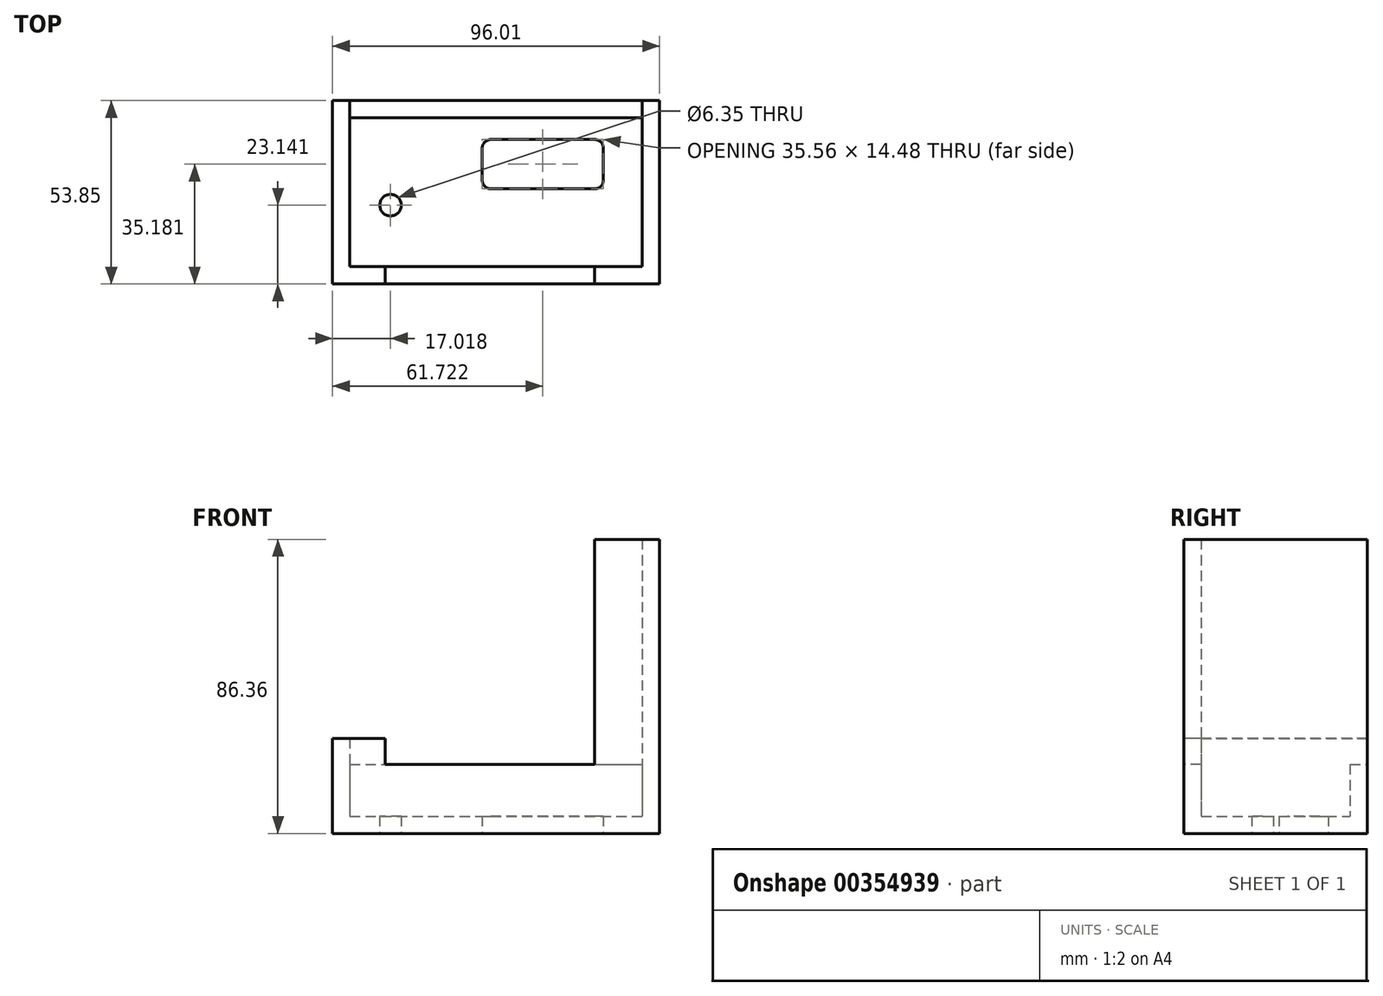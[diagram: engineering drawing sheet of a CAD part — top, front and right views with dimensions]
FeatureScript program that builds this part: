
annotation { "Feature Type Name" : "Feature", "Feature Type Description" : "" }
export const myFeature = defineFeature(function(context is Context, id is Id, definition is map)
    precondition{}
    {
        {
            var Q0;
            Q0=qCreatedBy(makeId("Front.planeOp"),FACE);
            var sketch = newSketch(context, id + "F0", { "sketchPlane" : qUnion([Q0])});
            skLineSegment(sketch, "E0.bottom", {"start": v(0, 86.36) * mm, "end": v(96.01, 86.36) * mm});
            skLineSegment(sketch, "E0.top", {"start": v(0, 0) * mm, "end": v(96.01, 0) * mm});
            skLineSegment(sketch, "E0.left", {"start": v(0, 86.36) * mm, "end": v(0, 0) * mm});
            skLineSegment(sketch, "E0.right", {"start": v(96.01, 86.36) * mm, "end": v(96.01, 0) * mm});
            skSolve(sketch);
        }
        {
            var Q0;
            Q0=makeQuery(id+"F0.imprint","IMPRINT",FACE,{"disambiguationData":[TD([[makeQuery(id+"F0.imprint","IMPRINT",EDGE,{"derivedFrom":sQuery(id+"F0.wireOp",EDGE,"E0.bottom")}),-1.0]])]});
            extrude(context, id + "F1", {"entities" : qUnion([Q0]), "depth" : 53.85 * mm});
        }
        {
            var Q0;
            Q0=makeQuery(id+"F1.opExtrude","SWEPT_FACE",FACE,{"disambiguationData":[OSD([sQuery(id+"F0.wireOp",EDGE,"E0.bottom")])]});
            var Q1;
            Q1=makeQuery(id+"F1.opExtrude","CAP_FACE",FACE,{"disambiguationData":[OSD([sQuery(id+"F0.wireOp",EDGE,"E0.bottom"),sQuery(id+"F0.wireOp",EDGE,"E0.top"),sQuery(id+"F0.wireOp",EDGE,"E0.left"),sQuery(id+"F0.wireOp",EDGE,"E0.right")])],"isStart":true});
            shell(context, id + "F2", {"entities" : qUnion([Q0, Q1]), "thickness" : 5.08 * mm});
        }
        {
            var Q0;
            Q0=makeQuery(id+"F1.opExtrude","SWEPT_FACE",FACE,{"disambiguationData":[OSD([sQuery(id+"F0.wireOp",EDGE,"E0.top")])]});
            var sketch = newSketch(context, id + "F3", { "sketchPlane" : qUnion([Q0])});
            skPoint(sketch, "E1", {"position": v(17.02, 30.7) * mm});
            skSolve(sketch);
        }
        {
            var Q0;
            Q0=sQuery(id+"F3.wireOp",VERTEX,"E1");
            var Q1;
            Q1=makeQuery(id+"F1.opExtrude","SWEPT_BODY",BODY,{"disambiguationData":[OSD([sQuery(id+"F0.wireOp",EDGE,"E0.bottom"),sQuery(id+"F0.wireOp",EDGE,"E0.top"),sQuery(id+"F0.wireOp",EDGE,"E0.left"),sQuery(id+"F0.wireOp",EDGE,"E0.right")])]});
            hole(context, id + "F4", {"style" : HoleStyle.SIMPLE, "endStyle" : HoleEndStyle.THROUGH, "holeDiameter" : 6.35 * mm, "isTappedThrough" : true, "tappedDepth" : 12.7 * mm, "tapClearance" : 3, "locations" : qUnion([Q0]), "scope" : qUnion([Q1])});
        }
        {
            var Q0;
            Q0=makeQuery(id+"F1.opExtrude","SWEPT_FACE",FACE,{"disambiguationData":[OSD([sQuery(id+"F0.wireOp",EDGE,"E0.top")])]});
            var sketch = newSketch(context, id + "F5", { "sketchPlane" : qUnion([Q0])});
            skLineSegment(sketch, "E2.bottom", {"start": v(46.48, 25.9) * mm, "end": v(76.96, 25.9) * mm});
            skLineSegment(sketch, "E2.top", {"start": v(46.48, 11.43) * mm, "end": v(76.96, 11.43) * mm});
            skLineSegment(sketch, "E2.left", {"start": v(43.94, 23.37) * mm, "end": v(43.94, 13.97) * mm});
            skLineSegment(sketch, "E2.right", {"start": v(79.5, 23.37) * mm, "end": v(79.5, 13.97) * mm});
            skPoint(sketch, "E3.visualSharp", {"position": v(43.94, 25.9) * mm});
            skArc(sketch, "E3.filletArc", {"start": v(46.48, 25.9) * mm, "mid": v(44.69, 25.16) * mm, "end": v(43.94, 23.37) * mm});
            skPoint(sketch, "E4.visualSharp", {"position": v(79.5, 11.43) * mm});
            skArc(sketch, "E4.filletArc", {"start": v(76.96, 11.43) * mm, "mid": v(78.76, 12.17) * mm, "end": v(79.5, 13.97) * mm});
            skPoint(sketch, "E5.visualSharp", {"position": v(79.5, 25.9) * mm});
            skArc(sketch, "E5.filletArc", {"start": v(79.5, 23.37) * mm, "mid": v(78.76, 25.16) * mm, "end": v(76.96, 25.9) * mm});
            skPoint(sketch, "E6.visualSharp", {"position": v(43.94, 11.43) * mm});
            skArc(sketch, "E6.filletArc", {"start": v(43.94, 13.97) * mm, "mid": v(44.69, 12.17) * mm, "end": v(46.48, 11.43) * mm});
            skSolve(sketch);
        }
        {
            var Q0;
            Q0 = qSketchRegion(id + "F5", true);
            var Q1;
            Q1 = qSketchRegion(id + "F9", true);
            extrude(context, id + "F6", {"entities" : qUnion([Q0, Q1]), "operationType" : NewBodyOperationType.REMOVE, "oppositeDirection" : true, "depth" : 25.4 * mm});
        }
        {
            var Q0;
            Q0=makeQuery(id+"F1.opExtrude","CAP_FACE",FACE,{"disambiguationData":[OSD([sQuery(id+"F0.wireOp",EDGE,"E0.bottom"),sQuery(id+"F0.wireOp",EDGE,"E0.top"),sQuery(id+"F0.wireOp",EDGE,"E0.left"),sQuery(id+"F0.wireOp",EDGE,"E0.right")])],"isStart":false});
            var sketch = newSketch(context, id + "F7", { "sketchPlane" : qUnion([Q0])});
            skLineSegment(sketch, "E7.bottom", {"start": v(5.33, 86.36) * mm, "end": v(89.66, 86.36) * mm});
            skLineSegment(sketch, "E7.top", {"start": v(5.33, 20.32) * mm, "end": v(89.66, 20.32) * mm});
            skLineSegment(sketch, "E7.left", {"start": v(5.33, 86.36) * mm, "end": v(5.33, 20.32) * mm});
            skLineSegment(sketch, "E7.right", {"start": v(89.66, 86.36) * mm, "end": v(89.66, 20.32) * mm});
            skSolve(sketch);
        }
        {
            var Q0;
            Q0 = qSketchRegion(id + "F7", true);
            extrude(context, id + "F8", {"entities" : qUnion([Q0]), "operationType" : NewBodyOperationType.REMOVE, "oppositeDirection" : true, "depth" : 25.4 * mm});
        }
        {
            var Q0;
            Q0=makeQuery(id+"F1.opExtrude","SWEPT_FACE",FACE,{"disambiguationData":[OSD([sQuery(id+"F0.wireOp",EDGE,"E0.left")])]});
            var sketch = newSketch(context, id + "F9", { "sketchPlane" : qUnion([Q0])});
            skLineSegment(sketch, "E8.bottom", {"start": v(0, 86.36) * mm, "end": v(53.85, 86.36) * mm});
            skLineSegment(sketch, "E8.top", {"start": v(0, 27.94) * mm, "end": v(53.85, 27.94) * mm});
            skLineSegment(sketch, "E8.left", {"start": v(0, 86.36) * mm, "end": v(0, 27.94) * mm});
            skLineSegment(sketch, "E8.right", {"start": v(53.85, 86.36) * mm, "end": v(53.85, 27.94) * mm});
            skSolve(sketch);
        }
        {
            var Q0;
            Q0 = qSketchRegion(id + "F9", true);
            extrude(context, id + "F10", {"entities" : qUnion([Q0]), "operationType" : NewBodyOperationType.REMOVE, "oppositeDirection" : true, "depth" : 25.4 * mm});
        }
        {
            var Q0;
            Q0=makeQuery(id+"F2.opShell","OFFSET_FACE",FACE,{"disambiguationData":[OSD([sQuery(id+"F0.wireOp",EDGE,"E0.top")])]});
            var sketch = newSketch(context, id + "F11", { "sketchPlane" : qUnion([Q0])});
            skLineSegment(sketch, "E9.bottom", {"start": v(5.08, 0) * mm, "end": v(90.93, 0) * mm});
            skLineSegment(sketch, "E9.top", {"start": v(5.08, -5.08) * mm, "end": v(90.93, -5.08) * mm});
            skLineSegment(sketch, "E9.left", {"start": v(5.08, 0) * mm, "end": v(5.08, -5.08) * mm});
            skLineSegment(sketch, "E9.right", {"start": v(90.93, 0) * mm, "end": v(90.93, -5.08) * mm});
            skSolve(sketch);
        }
        {
            var Q0;
            Q0 = qSketchRegion(id + "F11", true);
            extrude(context, id + "F12", {"entities" : qUnion([Q0]), "operationType" : NewBodyOperationType.ADD, "depth" : 15.24 * mm});
        }
        {
            var Q0;
            Q0=makeQuery(id+"F8.boolean.opBoolean","COPY",FACE,{"derivedFrom":makeQuery(id+"F8.opExtrude","SWEPT_FACE",FACE,{"disambiguationData":[OSD([sQuery(id+"F7.wireOp",EDGE,"E7.left")])]})});
            extrude(context, id + "F13", {"entities" : qUnion([Q0]), "operationType" : NewBodyOperationType.ADD, "depth" : 10.16 * mm});
        }
        {
            var Q0;
            Q0=makeQuery(id+"F8.boolean.opBoolean","COPY",FACE,{"derivedFrom":makeQuery(id+"F8.opExtrude","SWEPT_FACE",FACE,{"disambiguationData":[OSD([sQuery(id+"F7.wireOp",EDGE,"E7.right")])]})});
            extrude(context, id + "F14", {"entities" : qUnion([Q0]), "operationType" : NewBodyOperationType.ADD, "depth" : 12.7 * mm});
        }
    });
